# Revit family: P200635WX-129c_WUB50X24H_VZ
name_source: partatom
category: Specialty Equipment
units: mm (PartAtom-declared; Revit-internal decimal feet)

## family parameters
Always vertical = Yes
Cut with Voids When Loaded = No
Enable Cutting in Views = No
Maintain Annotation Orientation = No
Part Type = Normal
Room Calculation Point = No
Round Connector Dimension = Use Diameter
Shared = No
Work Plane-Based = No

## types (2) — shared parameters
Amps = 0 A
Back Panel Material = ARCAT - Metal - Aluminum
Body Material = ARCAT - Metal - Steel - Black
Clearance Material = ARCAT - Clearance
Default Elevation = 0"
Depth = 25 5/8"
Description = 24-inch Wide Undercounter Beverage Center - 5.2 cu. ft.
Centre de rafraîchissement sous le comptoir, 5.2 pi³
Dimension Guide = http://access.whirlpool.com Guide&sku=WUB50X24HV&language=EN
http://access.whirlpool.com Guide&sku=WUB50X24HV&language=EN
Display Panel Material = ARCAT - Metal - Cast Iron 1/4" Plate
Energy Guide = http://access.whirlpool.com Guide&sku=WUB50X24HV&language=EN
http://access.whirlpool.com Guide&sku=WUB50X24HV&language=EN
Family Name = Beverage Center
Feature 1 = LED Interior Lighting
Éclairage intérieur à DEL
Feature 2 = Wine Storage
Rangement pour le vin
Feature 3 = Dual-Temperature Controlled Zone
Deux zones à température contrôlée
Glass Material = ARCAT - Glass - Tempered - Black
Height = 35"
Leg Material = ARCAT - Plastic - Black
Manufacturer = Whirlpool
Rack Material = ARCAT - Metal - Cast Iron 1/4" Plate
Voltage = 0 V
Width = 23 15/16"

## per-type parameters (varying)
| type | Accent Material | Door Material | Handle Material |
| WUB50X24HZ | ARCAT - Metal - Steel - Stainless | ARCAT - Metal - Steel - Stainless | ARCAT - Metal - Steel - Grey |
| WUB50X24HV | ARCAT - Metal - Steel - Black | ARCAT - Metal - Steel - Stainless - Black | ARCAT - Metal - Steel - Stainless - Grey |

note: column(s) folded — value = type name in every type: Model

## geometry (parser evidence)
native form markers: Sweep x8
no freeform markers — native parametric forms only
